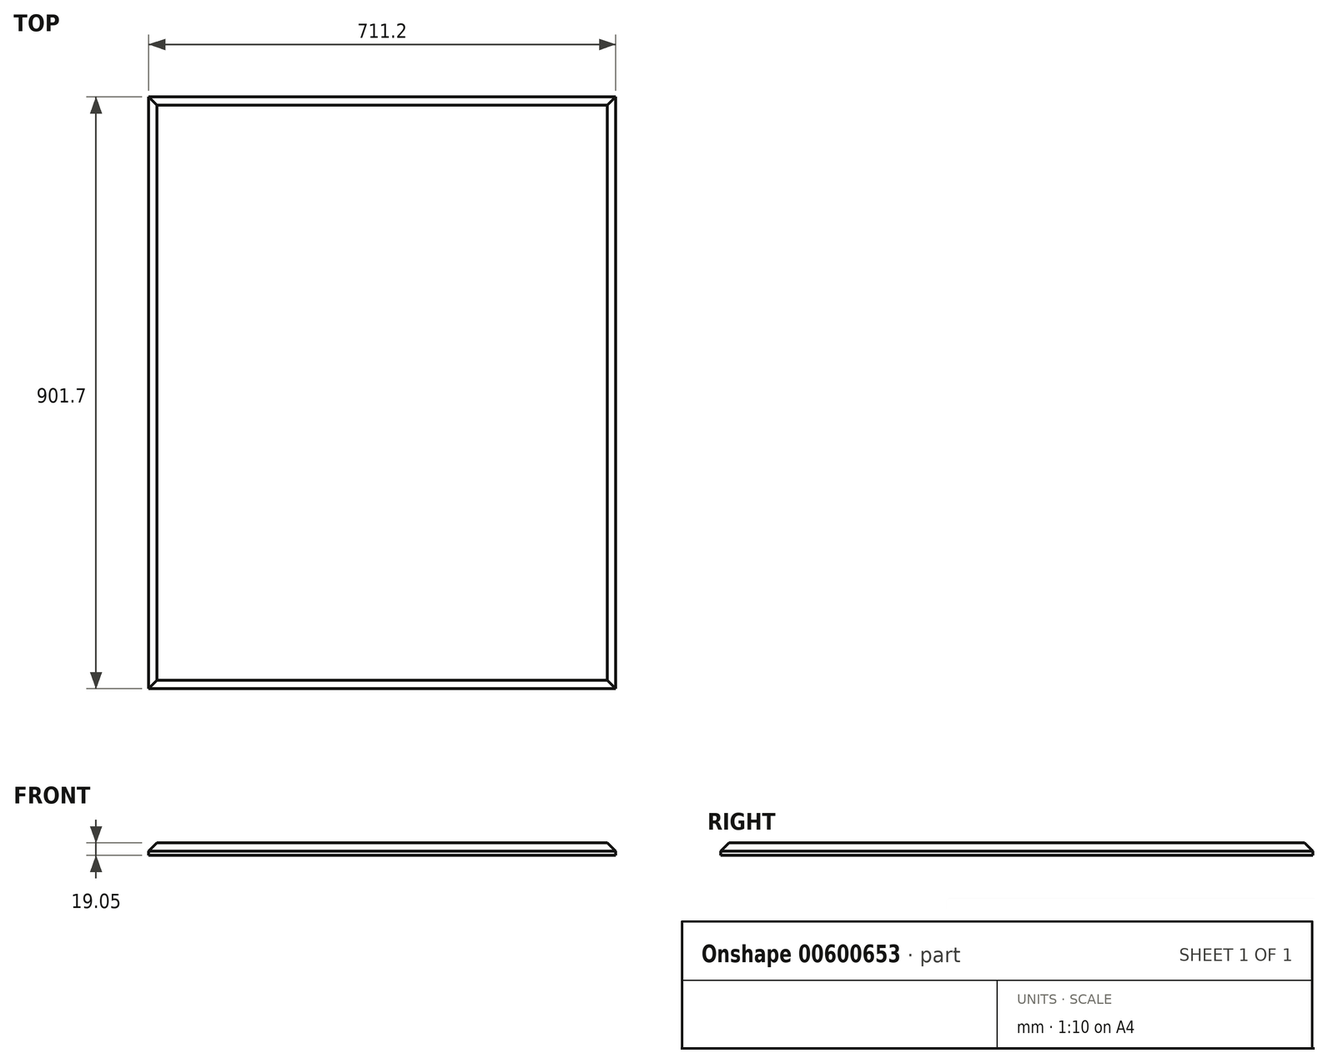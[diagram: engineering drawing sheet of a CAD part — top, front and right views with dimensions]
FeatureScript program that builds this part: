
annotation { "Feature Type Name" : "Feature", "Feature Type Description" : "" }
export const myFeature = defineFeature(function(context is Context, id is Id, definition is map)
    precondition{}
    {
        {
            var Q0;
            Q0=qCreatedBy(makeId("Top.planeOp"),FACE);
            var sketch = newSketch(context, id + "F0", { "sketchPlane" : qUnion([Q0])});
            skLineSegment(sketch, "E0.bottom", {"start": v(-355.6, 450.85) * mm, "end": v(355.6, 450.85) * mm});
            skLineSegment(sketch, "E0.top", {"start": v(-355.6, -450.85) * mm, "end": v(355.6, -450.85) * mm});
            skLineSegment(sketch, "E0.left", {"start": v(-355.6, 450.85) * mm, "end": v(-355.6, -450.85) * mm});
            skLineSegment(sketch, "E0.right", {"start": v(355.6, 450.85) * mm, "end": v(355.6, -450.85) * mm});
            skPoint(sketch, "E0.middle", {"position": v(0, 0) * mm});
            skSolve(sketch);
        }
        {
            var Q0;
            Q0=makeQuery(id+"F0.imprint","IMPRINT",FACE,{"disambiguationData":[TD([[makeQuery(id+"F0.imprint","IMPRINT",EDGE,{"derivedFrom":sQuery(id+"F0.wireOp",EDGE,"E0.bottom")}),-1.0]])]});
            extrude(context, id + "F1", {"entities" : qUnion([Q0]), "depth" : 19.05 * mm, "offsetDistance" : 25.4 * mm});
        }
        {
            var Q0;
            Q0=makeQuery(id+"F1.opExtrude","CAP_EDGE",EDGE,{"disambiguationData":[OSD([sQuery(id+"F0.wireOp",EDGE,"E0.left")])],"isStart":false});
            var Q1;
            Q1=makeQuery(id+"F1.opExtrude","CAP_EDGE",EDGE,{"disambiguationData":[OSD([sQuery(id+"F0.wireOp",EDGE,"E0.top")])],"isStart":false});
            var Q2;
            Q2=makeQuery(id+"F1.opExtrude","CAP_EDGE",EDGE,{"disambiguationData":[OSD([sQuery(id+"F0.wireOp",EDGE,"E0.right")])],"isStart":false});
            var Q3;
            Q3=makeQuery(id+"F1.opExtrude","CAP_EDGE",EDGE,{"disambiguationData":[OSD([sQuery(id+"F0.wireOp",EDGE,"E0.bottom")])],"isStart":false});
            chamfer(context, id + "F2", {"entities" : qUnion([Q0, Q1, Q2, Q3]), "width" : 12.7 * mm, "tangentPropagation" : true});
        }
    });
